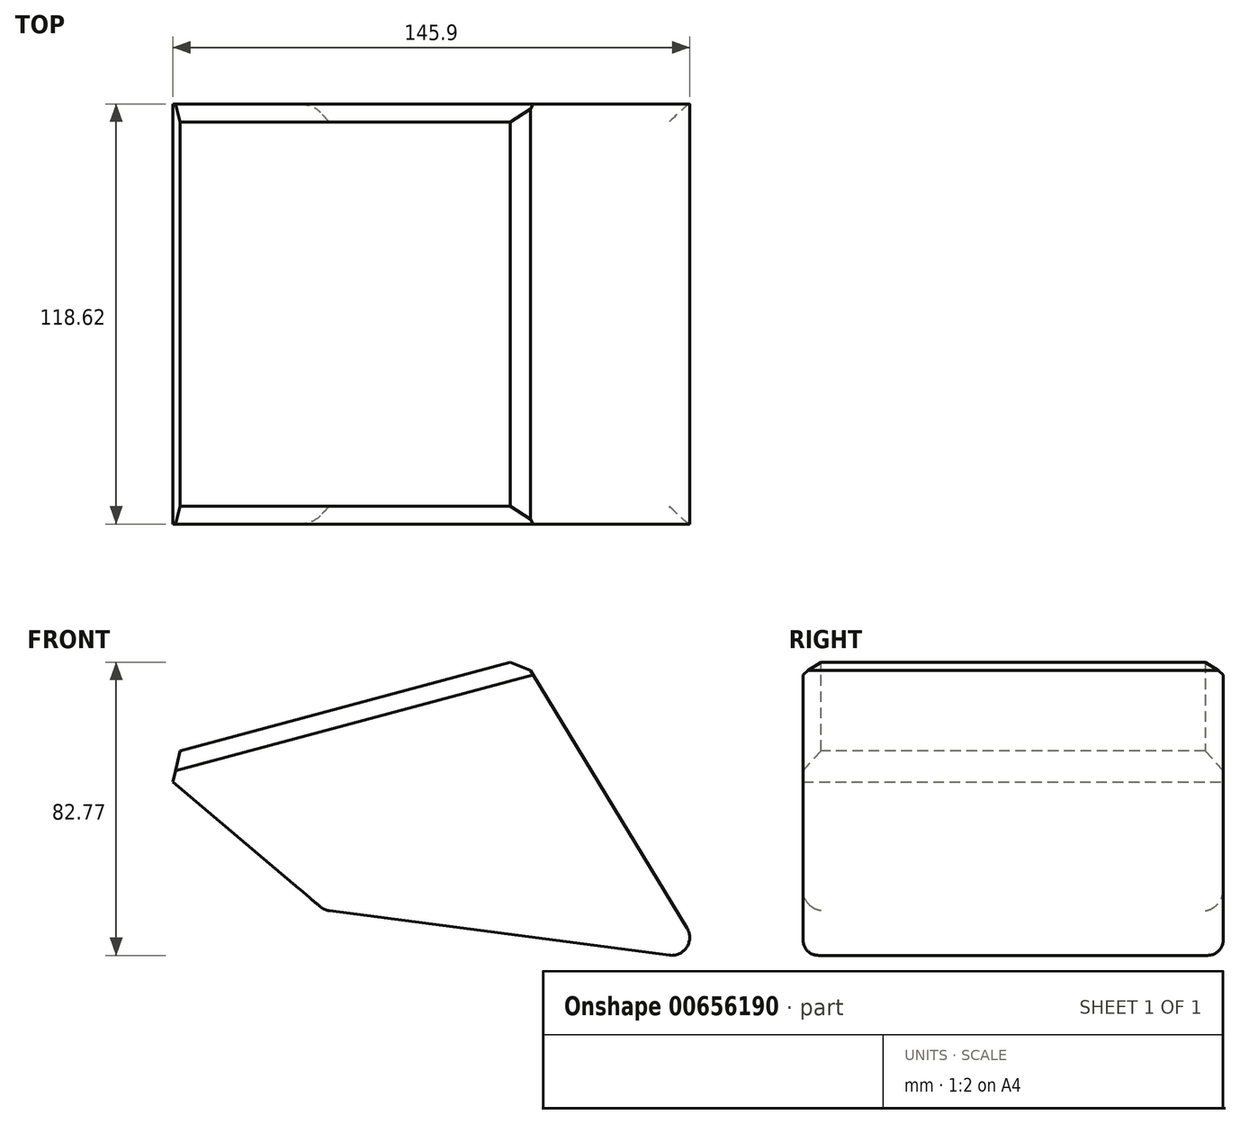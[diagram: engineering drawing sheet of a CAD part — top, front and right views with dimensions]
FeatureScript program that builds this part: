
annotation { "Feature Type Name" : "Feature", "Feature Type Description" : "" }
export const myFeature = defineFeature(function(context is Context, id is Id, definition is map)
    precondition{}
    {
        {
            var Q0;
            Q0=qCreatedBy(makeId("Front.planeOp"),FACE);
            var sketch = newSketch(context, id + "F0", { "sketchPlane" : qUnion([Q0])});
            skLineSegment(sketch, "E0", {"start": v(0, 0) * mm, "end": v(-50.16, 42.42) * mm});
            skLineSegment(sketch, "E1", {"start": v(-50.16, 42.42) * mm, "end": v(56.2, 70.95) * mm});
            skLineSegment(sketch, "E2", {"start": v(56.2, 70.95) * mm, "end": v(107.93, -14.14) * mm});
            skLineSegment(sketch, "E3", {"start": v(107.93, -14.14) * mm, "end": v(0, 0) * mm});
            skSolve(sketch);
        }
        {
            var Q0;
            Q0=makeQuery(id+"F0.imprint","IMPRINT",FACE,{"disambiguationData":[TD([[makeQuery(id+"F0.imprint","IMPRINT",EDGE,{"derivedFrom":sQuery(id+"F0.wireOp",EDGE,"E0")}),-1.0]])]});
            extrude(context, id + "F1", {"entities" : qUnion([Q0]), "depth" : 118.62 * mm, "offsetDistance" : 25.4 * mm});
        }
        {
            var Q0;
            Q0=makeQuery(id+"F1.opExtrude","SWEPT_FACE",FACE,{"disambiguationData":[OSD([sQuery(id+"F0.wireOp",EDGE,"E3")])]});
            var Q1;
            Q1=makeQuery(id+"F1.opExtrude","SWEPT_EDGE",EDGE,{"disambiguationData":[OSD([sQuery(id+"F0.wireOp",EDGE,"E2"),sQuery(id+"F0.wireOp",EDGE,"E3")])]});
            fillet(context, id + "F2", {"entities" : qUnion([Q0, Q1]), "radius" : 5.08 * mm, "tangentPropagation" : true, "allowEdgeOverflow" : false});
        }
        {
            var Q0;
            Q0=makeQuery(id+"F1.opExtrude","SWEPT_FACE",FACE,{"disambiguationData":[OSD([sQuery(id+"F0.wireOp",EDGE,"E1")])]});
            chamfer(context, id + "F3", {"entities" : qUnion([Q0]), "width" : 5.08 * mm, "tangentPropagation" : true});
        }
    });
